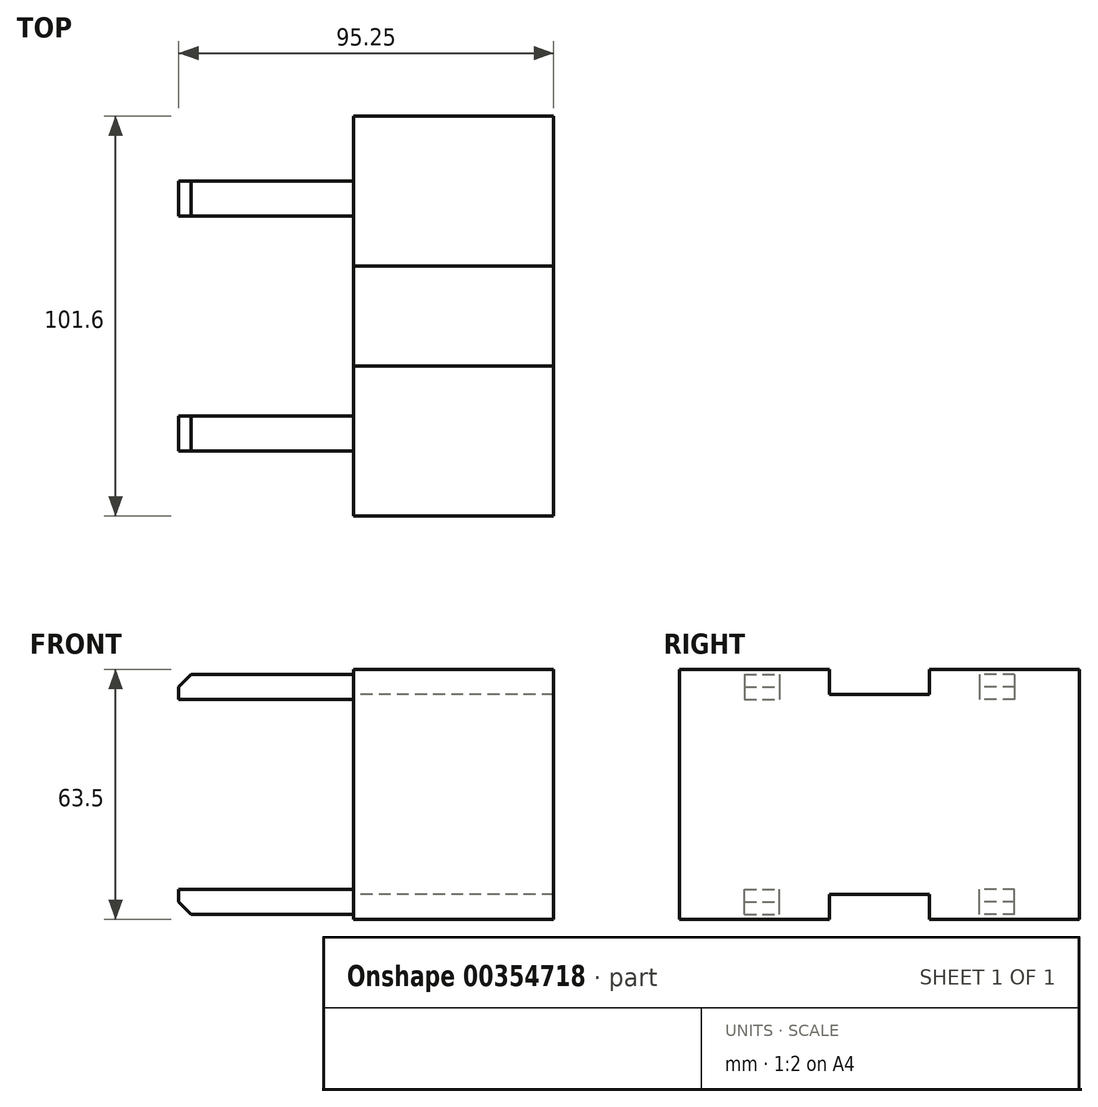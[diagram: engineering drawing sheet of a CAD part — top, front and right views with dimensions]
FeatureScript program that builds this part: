
annotation { "Feature Type Name" : "Feature", "Feature Type Description" : "" }
export const myFeature = defineFeature(function(context is Context, id is Id, definition is map)
    precondition{}
    {
        {
            var Q0;
            Q0=qCreatedBy(makeId("Right.planeOp"),FACE);
            var sketch = newSketch(context, id + "F0", { "sketchPlane" : qUnion([Q0])});
            skLineSegment(sketch, "E0", {"start": v(0, 25.4) * mm, "end": v(-12.7, 25.4) * mm});
            skLineSegment(sketch, "E1", {"start": v(-12.7, 25.4) * mm, "end": v(-12.7, 31.75) * mm});
            skLineSegment(sketch, "E2", {"start": v(-12.7, 31.75) * mm, "end": v(-50.8, 31.75) * mm});
            skLineSegment(sketch, "E3", {"start": v(-50.8, 31.75) * mm, "end": v(-50.8, 0) * mm});
            skLineSegment(sketch, "E4.MirrorCS", {"start": v(-50.8, -31.75) * mm, "end": v(-50.8, 0) * mm});
            skLineSegment(sketch, "E5.MirrorCS", {"start": v(-12.7, -31.75) * mm, "end": v(-50.8, -31.75) * mm});
            skLineSegment(sketch, "E6.MirrorCS", {"start": v(-12.7, -25.4) * mm, "end": v(-12.7, -31.75) * mm});
            skLineSegment(sketch, "E7.MirrorCS", {"start": v(0, -25.4) * mm, "end": v(-12.7, -25.4) * mm});
            skLineSegment(sketch, "E8.MirrorCS", {"start": v(0, 25.4) * mm, "end": v(12.7, 25.4) * mm});
            skLineSegment(sketch, "E9.MirrorCS", {"start": v(12.7, 25.4) * mm, "end": v(12.7, 31.75) * mm});
            skLineSegment(sketch, "E10.MirrorCS", {"start": v(0, -25.4) * mm, "end": v(12.7, -25.4) * mm});
            skLineSegment(sketch, "E11.MirrorCS", {"start": v(12.7, -25.4) * mm, "end": v(12.7, -31.75) * mm});
            skLineSegment(sketch, "E12.MirrorCS", {"start": v(12.7, 31.75) * mm, "end": v(50.8, 31.75) * mm});
            skLineSegment(sketch, "E13.MirrorCS", {"start": v(50.8, -31.75) * mm, "end": v(50.8, 0) * mm});
            skLineSegment(sketch, "E14.MirrorCS", {"start": v(12.7, -31.75) * mm, "end": v(50.8, -31.75) * mm});
            skLineSegment(sketch, "E15.MirrorCS", {"start": v(50.8, 31.75) * mm, "end": v(50.8, 0) * mm});
            skSolve(sketch);
        }
        {
            var Q0;
            Q0=makeQuery(id+"F0.imprint","IMPRINT",FACE,{"disambiguationData":[TD([[makeQuery(id+"F0.imprint","IMPRINT",EDGE,{"derivedFrom":sQuery(id+"F0.wireOp",EDGE,"E0")}),1.0]])]});
            extrude(context, id + "F1", {"entities" : qUnion([Q0]), "depth" : 50.8 * mm});
        }
        {
            var Q0;
            Q0=qCreatedBy(makeId("Front.planeOp"),FACE);
            var sketch = newSketch(context, id + "F2", { "sketchPlane" : qUnion([Q0])});
            skLineSegment(sketch, "E16", {"start": v(0, 25.4) * mm, "end": v(-41.28, 25.4) * mm});
            skLineSegment(sketch, "E17", {"start": v(-41.28, 25.4) * mm, "end": v(-44.45, 22.23) * mm});
            skLineSegment(sketch, "E18", {"start": v(-44.45, 22.22) * mm, "end": v(-44.45, 19.05) * mm});
            skLineSegment(sketch, "E19", {"start": v(-44.45, 19.05) * mm, "end": v(0, 19.05) * mm});
            skLineSegment(sketch, "E20", {"start": v(0, 25.4) * mm, "end": v(0, 19.05) * mm});
            skSolve(sketch);
        }
        {
            var Q0;
            Q0=makeQuery(id+"F2.imprint","IMPRINT",FACE,{"disambiguationData":[TD([[makeQuery(id+"F2.imprint","IMPRINT",EDGE,{"derivedFrom":sQuery(id+"F2.wireOp",EDGE,"E16")}),1.0]])]});
            extrude(context, id + "F3", {"entities" : qUnion([Q0]), "depth" : 8.9 * mm});
        }
        {
            var Q0;
            Q0=makeQuery(id+"F3.opExtrude","SWEPT_BODY",BODY,{"disambiguationData":[OSD([sQuery(id+"F2.wireOp",EDGE,"E16"),sQuery(id+"F2.wireOp",EDGE,"E17"),sQuery(id+"F2.wireOp",EDGE,"E18"),sQuery(id+"F2.wireOp",EDGE,"E19"),sQuery(id+"F2.wireOp",EDGE,"E20")])]});
            var Q1;
            Q1=qCreatedBy(makeId("Top.planeOp"),FACE);
            mirror(context, id + "F4", {"entities" : qUnion([Q0]), "mirrorPlane" : qUnion([Q1])});
        }
        {
            var Q0;
            Q0=makeQuery(id+"F3.opExtrude","SWEPT_BODY",BODY,{"disambiguationData":[OSD([sQuery(id+"F2.wireOp",EDGE,"E16"),sQuery(id+"F2.wireOp",EDGE,"E17"),sQuery(id+"F2.wireOp",EDGE,"E18"),sQuery(id+"F2.wireOp",EDGE,"E19"),sQuery(id+"F2.wireOp",EDGE,"E20")])]});
            var Q1;
            Q1=makeQuery(id+"F4.opPattern","COPY",BODY,{"derivedFrom":makeQuery(id+"F3.opExtrude","SWEPT_BODY",BODY,{"disambiguationData":[OSD([sQuery(id+"F2.wireOp",EDGE,"E16"),sQuery(id+"F2.wireOp",EDGE,"E17"),sQuery(id+"F2.wireOp",EDGE,"E18"),sQuery(id+"F2.wireOp",EDGE,"E19"),sQuery(id+"F2.wireOp",EDGE,"E20")])]}),"instanceName":"1"});
            var Q2;
            Q2=makeQuery(id+"F1.opExtrude","CAP_EDGE",EDGE,{"disambiguationData":[OSD([sQuery(id+"F0.wireOp",EDGE,"E2")])],"isStart":true});
            transform(context, id + "F5", {"entities" : qUnion([Q0, Q1]), "transformType" : TransformType.TRANSLATION_ENTITY, "oppositeDirectionEntity" : false, "transformLine" : qUnion([Q2]), "makeCopy" : false});
        }
        {
            var Q0;
            Q0=makeQuery(id+"F3.opExtrude","SWEPT_BODY",BODY,{"disambiguationData":[OSD([sQuery(id+"F2.wireOp",EDGE,"E16"),sQuery(id+"F2.wireOp",EDGE,"E17"),sQuery(id+"F2.wireOp",EDGE,"E18"),sQuery(id+"F2.wireOp",EDGE,"E19"),sQuery(id+"F2.wireOp",EDGE,"E20")])]});
            transform(context, id + "F6", {"entities" : qUnion([Q0]), "transformType" : TransformType.TRANSLATION_3D, "dx" : 0 * mm, "dy" : 0 * mm, "dz" : 5.08 * mm, "makeCopy" : false});
        }
        {
            var Q0;
            Q0=makeQuery(id+"F4.opPattern","COPY",BODY,{"derivedFrom":makeQuery(id+"F3.opExtrude","SWEPT_BODY",BODY,{"disambiguationData":[OSD([sQuery(id+"F2.wireOp",EDGE,"E16"),sQuery(id+"F2.wireOp",EDGE,"E17"),sQuery(id+"F2.wireOp",EDGE,"E18"),sQuery(id+"F2.wireOp",EDGE,"E19"),sQuery(id+"F2.wireOp",EDGE,"E20")])]}),"instanceName":"1"});
            transform(context, id + "F7", {"entities" : qUnion([Q0]), "transformType" : TransformType.TRANSLATION_3D, "dx" : 0 * mm, "dy" : 0 * mm, "dz" : -5.08 * mm, "makeCopy" : false});
        }
        {
            var Q0;
            Q0=makeQuery(id+"F3.opExtrude","SWEPT_BODY",BODY,{"disambiguationData":[OSD([sQuery(id+"F2.wireOp",EDGE,"E16"),sQuery(id+"F2.wireOp",EDGE,"E17"),sQuery(id+"F2.wireOp",EDGE,"E18"),sQuery(id+"F2.wireOp",EDGE,"E19"),sQuery(id+"F2.wireOp",EDGE,"E20")])]});
            var Q1;
            Q1=makeQuery(id+"F4.opPattern","COPY",BODY,{"derivedFrom":makeQuery(id+"F3.opExtrude","SWEPT_BODY",BODY,{"disambiguationData":[OSD([sQuery(id+"F2.wireOp",EDGE,"E16"),sQuery(id+"F2.wireOp",EDGE,"E17"),sQuery(id+"F2.wireOp",EDGE,"E18"),sQuery(id+"F2.wireOp",EDGE,"E19"),sQuery(id+"F2.wireOp",EDGE,"E20")])]}),"instanceName":"1"});
            var Q2;
            Q2=qCreatedBy(makeId("Front.planeOp"),FACE);
            mirror(context, id + "F8", {"entities" : qUnion([Q0, Q1]), "mirrorPlane" : qUnion([Q2])});
        }
        {
            var Q0;
            Q0=makeQuery(id+"F3.opExtrude","SWEPT_BODY",BODY,{"disambiguationData":[OSD([sQuery(id+"F2.wireOp",EDGE,"E16"),sQuery(id+"F2.wireOp",EDGE,"E17"),sQuery(id+"F2.wireOp",EDGE,"E18"),sQuery(id+"F2.wireOp",EDGE,"E19"),sQuery(id+"F2.wireOp",EDGE,"E20")])]});
            var Q1;
            Q1=makeQuery(id+"F4.opPattern","COPY",BODY,{"derivedFrom":makeQuery(id+"F3.opExtrude","SWEPT_BODY",BODY,{"disambiguationData":[OSD([sQuery(id+"F2.wireOp",EDGE,"E16"),sQuery(id+"F2.wireOp",EDGE,"E17"),sQuery(id+"F2.wireOp",EDGE,"E18"),sQuery(id+"F2.wireOp",EDGE,"E19"),sQuery(id+"F2.wireOp",EDGE,"E20")])]}),"instanceName":"1"});
            transform(context, id + "F9", {"entities" : qUnion([Q0, Q1]), "transformType" : TransformType.TRANSLATION_3D, "dx" : 0 * mm, "dy" : 12.7 * mm, "dz" : 0 * mm, "makeCopy" : false});
        }
        {
            var Q0;
            Q0=makeQuery(id+"F8.opPattern","COPY",BODY,{"derivedFrom":makeQuery(id+"F3.opExtrude","SWEPT_BODY",BODY,{"disambiguationData":[OSD([sQuery(id+"F2.wireOp",EDGE,"E16"),sQuery(id+"F2.wireOp",EDGE,"E17"),sQuery(id+"F2.wireOp",EDGE,"E18"),sQuery(id+"F2.wireOp",EDGE,"E19"),sQuery(id+"F2.wireOp",EDGE,"E20")])]}),"instanceName":"1"});
            var Q1;
            Q1=makeQuery(id+"F8.opPattern","COPY",BODY,{"derivedFrom":makeQuery(id+"F4.opPattern","COPY",BODY,{"derivedFrom":makeQuery(id+"F3.opExtrude","SWEPT_BODY",BODY,{"disambiguationData":[OSD([sQuery(id+"F2.wireOp",EDGE,"E16"),sQuery(id+"F2.wireOp",EDGE,"E17"),sQuery(id+"F2.wireOp",EDGE,"E18"),sQuery(id+"F2.wireOp",EDGE,"E19"),sQuery(id+"F2.wireOp",EDGE,"E20")])]}),"instanceName":"1"}),"instanceName":"1"});
            transform(context, id + "F10", {"entities" : qUnion([Q0, Q1]), "transformType" : TransformType.TRANSLATION_3D, "dx" : 0 * mm, "dy" : -12.7 * mm, "dz" : 0 * mm, "makeCopy" : false});
        }
    });
